# Revit family: FXP_A3-Bath-(1)
name_source: partatom
category: Plumbing Fixtures
revit_build: Autodesk Revit 2016 (Build: 20150220_1215(x64)
units: mm (PartAtom-declared; Revit-internal decimal feet)

## family parameters
Always vertical = Yes
Cut with Voids When Loaded = No
Part Type = Normal
Room Calculation Point = No
Round Connector Dimension = Use Diameter
Shared = No
Work Plane-Based = No

## types (3) — shared parameters
Assembly Code = D2010510
Keynote = N13/220
Manufacturer = Revit
Material Bath = Porcelain

## per-type parameters (varying)
| type | Length | Width |
| Bath 1675 x 915 mm | 1675 mm  [stored 5.49541 ft] | 915 mm  [stored 3.00197 ft] |
| Bath 1475 x 755mm | 1475 mm  [stored 4.83924 ft] | 755 mm  [stored 2.47703 ft] |
| Bath 1575 x 815mm | 1575 mm  [stored 5.16732 ft] | 815 mm  [stored 2.67388 ft] |

note: [stored X ft] marks values corroborated as IEEE doubles in the binary element streams (Revit-internal decimal feet)

## geometry (parser evidence)
native form markers: Sweep x2
no freeform markers — native parametric forms only
